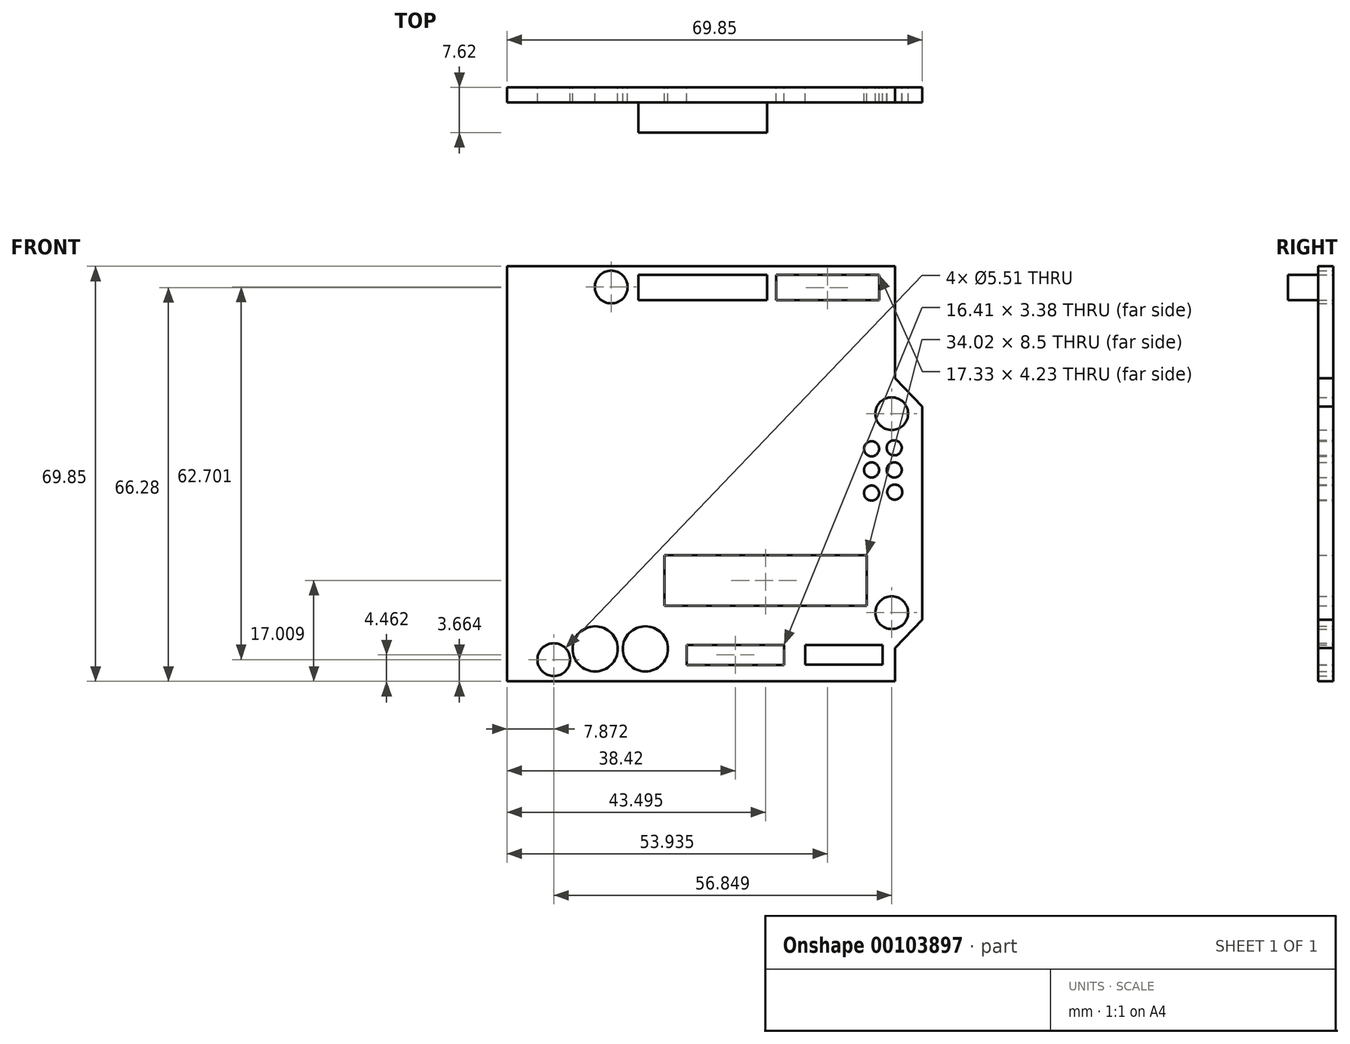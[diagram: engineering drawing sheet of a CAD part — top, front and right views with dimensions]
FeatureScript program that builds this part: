
annotation { "Feature Type Name" : "Feature", "Feature Type Description" : "" }
export const myFeature = defineFeature(function(context is Context, id is Id, definition is map)
    precondition{}
    {
        {
            var Q0;
            Q0=qCreatedBy(makeId("Front.planeOp"),FACE);
            var sketch = newSketch(context, id + "F0", { "sketchPlane" : qUnion([Q0])});
            skLineSegment(sketch, "E0.bottom", {"start": v(-69.85, 42.38) * mm, "end": v(-4.57, 42.38) * mm});
            skLineSegment(sketch, "E0.top", {"start": v(-69.85, -27.47) * mm, "end": v(-4.57, -27.47) * mm});
            skLineSegment(sketch, "E0.left", {"start": v(-69.85, 42.38) * mm, "end": v(-69.85, -27.47) * mm});
            skLineSegment(sketch, "E0.right", {"start": v(-4.57, 42.38) * mm, "end": v(-4.57, 23.56) * mm});
            skLineSegment(sketch, "E1.trimOffspring", {"start": v(-4.57, -21.88) * mm, "end": v(-4.57, -27.47) * mm});
            skLineSegment(sketch, "E2", {"start": v(0, 18.77) * mm, "end": v(0, -17.09) * mm});
            skLineSegment(sketch, "E3", {"start": v(-4.57, -21.88) * mm, "end": v(0, -17.09) * mm});
            skLineSegment(sketch, "E4", {"start": v(-4.57, 23.56) * mm, "end": v(0, 18.77) * mm});
            skLineSegment(sketch, "E5.bottom", {"start": v(-47.75, 40.92) * mm, "end": v(-26.1, 40.92) * mm});
            skLineSegment(sketch, "E5.top", {"start": v(-47.75, 36.7) * mm, "end": v(-26.1, 36.7) * mm});
            skLineSegment(sketch, "E5.left", {"start": v(-47.75, 40.92) * mm, "end": v(-47.75, 36.7) * mm});
            skLineSegment(sketch, "E5.right", {"start": v(-26.1, 40.92) * mm, "end": v(-26.1, 36.7) * mm});
            skLineSegment(sketch, "E6.bottom", {"start": v(-24.58, 40.92) * mm, "end": v(-7.25, 40.92) * mm});
            skLineSegment(sketch, "E6.top", {"start": v(-24.58, 36.7) * mm, "end": v(-7.25, 36.7) * mm});
            skLineSegment(sketch, "E6.left", {"start": v(-24.58, 40.92) * mm, "end": v(-24.58, 36.7) * mm});
            skLineSegment(sketch, "E6.right", {"start": v(-7.25, 40.92) * mm, "end": v(-7.25, 36.7) * mm});
            skCircle(sketch, "E7", {"center": v(-5.13, 17.58) * mm, "radius": 2.75 * mm});
            skCircle(sketch, "E8", {"center": v(-5.13, -15.9) * mm, "radius": 2.75 * mm});
            skCircle(sketch, "E9", {"center": v(-52.32, 38.9) * mm, "radius": 2.76 * mm});
            skCircle(sketch, "E10", {"center": v(-4.7, 11.83) * mm, "radius": 1.27 * mm});
            skCircle(sketch, "E11", {"center": v(-4.7, 8.11) * mm, "radius": 1.27 * mm});
            skCircle(sketch, "E12", {"center": v(-4.62, 4.4) * mm, "radius": 1.27 * mm});
            skCircle(sketch, "E13", {"center": v(-8.52, 4.22) * mm, "radius": 1.27 * mm});
            skCircle(sketch, "E14", {"center": v(-8.52, 8.11) * mm, "radius": 1.27 * mm});
            skCircle(sketch, "E15", {"center": v(-8.52, 11.68) * mm, "radius": 1.27 * mm});
            skPoint(sketch, "E16.oppositeSnap0", {"position": v(-4.57, -24.67) * mm});
            skLineSegment(sketch, "E16.bottom", {"start": v(-19.68, -21.32) * mm, "end": v(-6.65, -21.32) * mm});
            skLineSegment(sketch, "E16.top", {"start": v(-19.68, -24.67) * mm, "end": v(-6.65, -24.67) * mm});
            skLineSegment(sketch, "E16.left", {"start": v(-19.68, -21.32) * mm, "end": v(-19.68, -24.67) * mm});
            skLineSegment(sketch, "E16.right", {"start": v(-6.65, -21.32) * mm, "end": v(-6.65, -24.67) * mm});
            skLineSegment(sketch, "E17.bottom", {"start": v(-23.23, -21.32) * mm, "end": v(-39.63, -21.32) * mm});
            skLineSegment(sketch, "E17.top", {"start": v(-23.23, -24.7) * mm, "end": v(-39.63, -24.7) * mm});
            skLineSegment(sketch, "E17.left", {"start": v(-23.23, -21.32) * mm, "end": v(-23.23, -24.7) * mm});
            skLineSegment(sketch, "E17.right", {"start": v(-39.63, -21.32) * mm, "end": v(-39.63, -24.7) * mm});
            skCircle(sketch, "E18", {"center": v(-46.57, -22) * mm, "radius": 3.8 * mm});
            skCircle(sketch, "E19", {"center": v(-55.02, -22) * mm, "radius": 3.8 * mm});
            skCircle(sketch, "E20", {"center": v(-61.98, -23.8) * mm, "radius": 2.76 * mm});
            skLineSegment(sketch, "E21.bottom", {"start": v(-43.36, -6.2) * mm, "end": v(-9.35, -6.2) * mm});
            skLineSegment(sketch, "E21.top", {"start": v(-43.36, -14.71) * mm, "end": v(-9.35, -14.71) * mm});
            skLineSegment(sketch, "E21.left", {"start": v(-43.36, -6.2) * mm, "end": v(-43.36, -14.71) * mm});
            skLineSegment(sketch, "E21.right", {"start": v(-9.35, -6.2) * mm, "end": v(-9.35, -14.71) * mm});
            skSolve(sketch);
        }
        {
            var Q0;
            Q0=makeQuery(id+"F0.imprint","IMPRINT",FACE,{"disambiguationData":[TD([[makeQuery(id+"F0.imprint","IMPRINT",EDGE,{"derivedFrom":sQuery(id+"F0.wireOp",EDGE,"E0.bottom")}),-1.0]])]});
            var sketch = newSketch(context, id + "F1", { "sketchPlane" : qUnion([Q0])});
            skSolve(sketch);
        }
        {
            var Q0;
            Q0=makeQuery(id+"F1.imprint","IMPRINT",FACE,{"disambiguationData":[TD([[makeQuery(id+"F1.imprint","IMPRINT",EDGE,{"derivedFrom":makeQuery(id+"F0.imprint","IMPRINT",EDGE,{"derivedFrom":sQuery(id+"F0.wireOp",EDGE,"E0.bottom")})}),-1.0]])]});
            extrude(context, id + "F2", {"entities" : qUnion([Q0]), "depth" : 2.54 * mm});
        }
        {
            var Q0;
            Q0=makeQuery(id+"F0.imprint","IMPRINT",FACE,{"disambiguationData":[TD([[makeQuery(id+"F0.imprint","IMPRINT",EDGE,{"derivedFrom":sQuery(id+"F0.wireOp",EDGE,"E5.bottom")}),-1.0]])]});
            extrude(context, id + "F3", {"entities" : qUnion([Q0]), "operationType" : NewBodyOperationType.ADD, "depth" : 7.62 * mm});
        }
    });
